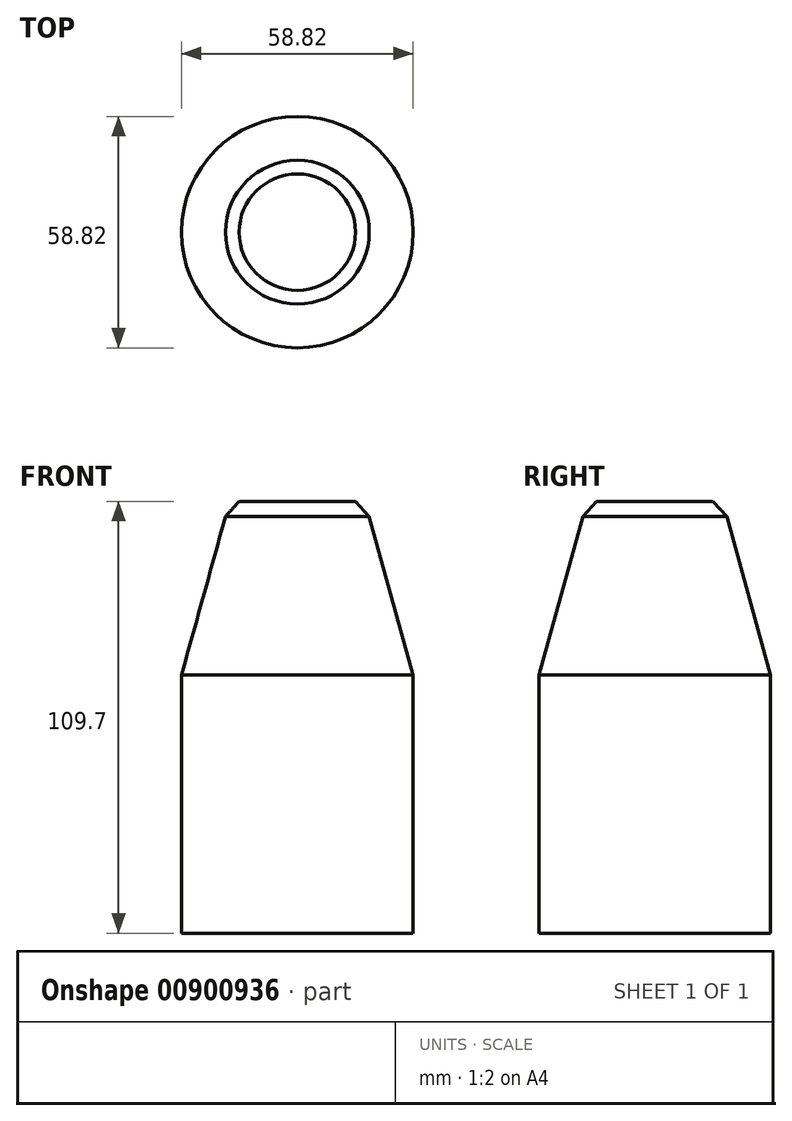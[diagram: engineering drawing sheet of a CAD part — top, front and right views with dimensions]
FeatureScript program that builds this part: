
annotation { "Feature Type Name" : "Feature", "Feature Type Description" : "" }
export const myFeature = defineFeature(function(context is Context, id is Id, definition is map)
    precondition{}
    {
        {
            var Q0;
            Q0=qCreatedBy(makeId("Front.planeOp"),FACE);
            var sketch = newSketch(context, id + "F0", { "sketchPlane" : qUnion([Q0])});
            skLineSegment(sketch, "E0", {"start": v(0, 44.1) * mm, "end": v(14.78, 44.1) * mm});
            skLineSegment(sketch, "E1", {"start": v(14.78, 44.1) * mm, "end": v(18.27, 40.27) * mm});
            skLineSegment(sketch, "E2", {"start": v(18.27, 40.27) * mm, "end": v(29.41, 0) * mm});
            skLineSegment(sketch, "E3", {"start": v(29.41, 0) * mm, "end": v(29.41, -2.92) * mm});
            skLineSegment(sketch, "E4", {"start": v(29.41, -2.92) * mm, "end": v(29.41, -65.6) * mm});
            skLineSegment(sketch, "E5", {"start": v(29.41, -65.6) * mm, "end": v(0, -65.6) * mm});
            skLineSegment(sketch, "E6", {"start": v(0, -65.6) * mm, "end": v(0, 44.1) * mm});
            skSolve(sketch);
        }
        {
            var Q0;
            Q0=makeQuery(id+"F0.imprint","IMPRINT",FACE,{"disambiguationData":[TD([[makeQuery(id+"F0.imprint","IMPRINT",EDGE,{"derivedFrom":sQuery(id+"F0.wireOp",EDGE,"E0")}),-1.0]])]});
            var Q1;
            Q1=sQuery(id+"F0.wireOp",EDGE,"E0");
            var Q2;
            Q2=sQuery(id+"F0.wireOp",EDGE,"E2");
            var Q3;
            Q3=sQuery(id+"F0.wireOp",EDGE,"E4");
            var Q4;
            Q4=sQuery(id+"F0.wireOp",EDGE,"E6");
            revolve(context, id + "F1", {"bodyType" : ToolBodyType.SURFACE, "surfaceOperationType" : NewSurfaceOperationType.NEW, "entities" : qUnion([Q0]), "surfaceEntities" : qUnion([Q1, Q2, Q3]), "axis" : qUnion([Q4]), "revolveType" : RevolveType.FULL});
        }
        {
            var Q0;
            Q0 = qSketchRegion(id + "F0", true);
            var Q1;
            Q1=sQuery(id+"F0.wireOp",EDGE,"E6");
            revolve(context, id + "F2", {"surfaceOperationType" : NewSurfaceOperationType.NEW, "entities" : qUnion([Q0]), "axis" : qUnion([Q1]), "revolveType" : RevolveType.FULL});
        }
    });
